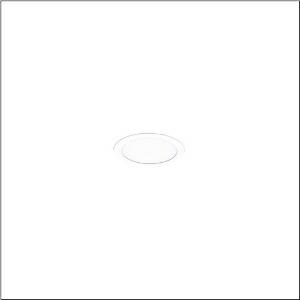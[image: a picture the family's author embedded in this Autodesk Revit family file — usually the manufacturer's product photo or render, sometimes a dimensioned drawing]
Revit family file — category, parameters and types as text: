
# Revit family: lunis_21_s_51db16ta91c
name_source: partatom
category: Lighting Fixtures
units: mm (PartAtom-declared; Revit-internal decimal feet)

## family parameters
Cut with Voids When Loaded = No
Host = Face
Light Source = No
Part Type = Normal
Room Calculation Point = No
Round Connector Dimension = Use Diameter
Shared = No

## types (1)
- --- (1 x LED 3000 K ... 6500 K, 1010 lm, 8 W, 4000K)
    Apparent Load = 8 VA
    CIE Flux Codes = 50 80 96 100 100
    Color Rendering = 80
    Color Temperature = 4000K
    Default Elevation = 1800 mm
    Description = Lunis 21 S, downlight, light control with lens, of PMMA, optical cover: cover panel, of PC, opal, light emission: direct distribution, LED rated luminous flux: 1.010lm, light colour: 8tw, with terminal, 5-pole, mains connection: 220..240V, AC, 50..60Hz, housing, round, of diecast aluminium, traffic white (RAL 9016), diameter: 84mm, clamping range: 1..40mm, protection rating (complete): IP20, protection rating (on room side): IP54, insulation class (complete): insulation class II (safety insulation), certification: CE, impact resistance: IK03, packaging unit: 1 piece
    Height = 0 mm  [stored 0 ft]
    Lamp = 1 x LED 3000 K ... 6500 K
    Lamp Light Flux = 1010 lm
    Lamp Power = 8 W
    Lamp count = 1
    Length = 84 mm
    Luminous efficacy = 126 lm/W
    Manufacturer = Siteco
    ModVariant = No
    Model = 51DB16TA91C
    Mounting Place = Ceiling
    Mounting Type = Recessed
    Number of Poles = 1
    OnlyDefault = Yes
    Power Factor = 1
    Product Name = Lunis 21 S
    Product group = downlight
    ProductGroupID = 401
    Protection Class = Protection class II
    Protection Degree = IP 20
    RLX_Detail_Level = 1
    RLX_Emergency_Light_Flux = 0 lm
    RLX_Emergency_Type = 0
    RLX_Emergency_Type_DB = No
    RlxData = <blob elided: 7797 chars, md5=8f91517b>
    Socket = socket
    Standby Power = 0 W
    System Light Flux = 1010 lm
    System Power = 8 W
    Type Comments = individual setting: CCT=4000K, colour temperature 4000K, luminous flux: 100 % | (OFF | OFF | ON | OFF) | 200 mA
    Type Image = l_1290838.jpg
    URL = http://relux.com
    VarID = @adj_034521
    Voltage = 0 V
    Weight = 0.00 kg
    Width = 0 mm  [stored 0 ft]

note: [stored X ft] marks values corroborated as IEEE doubles in the binary element streams (Revit-internal decimal feet)

## geometry (parser evidence)
native form markers: Sweep x9
no freeform markers — native parametric forms only
